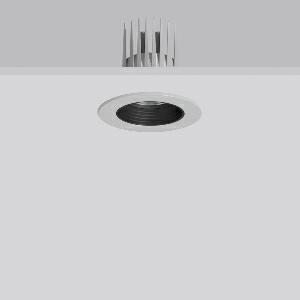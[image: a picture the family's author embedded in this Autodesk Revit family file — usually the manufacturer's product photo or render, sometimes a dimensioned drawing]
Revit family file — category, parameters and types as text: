
# Revit family: heledon_mini_e_901746_004_2_a7c6
name_source: partatom
category: Lighting Fixtures
units: mm (PartAtom-declared; Revit-internal decimal feet)

## family parameters
Cut with Voids When Loaded = No
Host = Face
Light Source = No
Part Type = Normal
Room Calculation Point = No
Round Connector Dimension = Use Diameter
Shared = No

## types (1)
- HELEDON mini E (1 x LED Modul 927, 2150 lm, 2700)
    Apparent Load = 20 VA
    Approval mark = CE
    CIE Flux Codes = 80 99 100 100 100
    Color Rendering = 92
    Color Temperature = 2700
    Default Elevation = 1800 mm
    Description = Series: HELEDON mini
Round recessed downlight. Housing: die-cast aluminium, powder-coated. Black plastic ring and recessed LED to prevent glare from the side. Optical assembly with lens made of plastic (polycarbonate) for the best homogeneous light distribution - can be changed without tools. Best colour rendering index Ra>90. Suitable for Recessed ceiling mounting. Installation without tools thanks to spring fastening system. Including separate LED converter with connecting cable 600 mm.High quality converter without flickering and stroboscopic effect. Through-wiring box (5 pole) available as accessory. The following accessories can be mounted without use of tools: interchangeable lenses, decorative glasses, honeycomb louvre, clear and frosted diffusers, white interchangeable plastic ring. 
Colour: silver
Diameter: 124 mm
Height: 3 mm
Cut-out diameter: 114 mm
Recess height: 170 mm
Luminaire: recess height: 120 mm
Lamp: LED
Socket: without socket
Colour temperature: 2700K
Colour rendering index (CRI): 92
System power: 20 W
Rated luminous flux: 2150 lm
Luminous efficiency: 108 lm/W
Control gear: Regulated power supply
Protection class: II
Type of protection: IP 20
    Height = 0 mm  [stored 0 ft]
    Lamp = 1 x LED Modul 927
    Lamp Light Flux = 2150 lm
    Lamp count = 1
    Length = 124 mm  [stored 0.406824 ft]
    Lifetime = 50000 h
    Luminous efficacy = 108 lm/W
    Manufacturer = RZB
    ModVariant = No
    Model = 901746.004.2
    Mounting Place = Ceiling
    Mounting Type = Recessed
    Number of Poles = 1
    OnlyDefault = Yes
    Power Factor = 1
    Product Name = HELEDON mini E
    Product group = Recessed downlights
    ProductGroupID = 402
    Protection Class = Protection class II
    Protection Degree = IP 20
    RLX_Detail_Level = 1
    RLX_Emergency_Light_Flux = 0 lm
    RLX_Emergency_Type = 0
    RLX_Emergency_Type_DB = No
    RlxData = <blob elided: 127645 chars, md5=7dd7c361>
    Socket = socket
    Standby Power = 0 W
    System Light Flux = 2150 lm
    System Power = 20 W
    Type Comments = Product without accessories
    Type Image = 901656.004.jpg
    URL = http://relux.com
    VarID = ---
    Voltage = 230 V
    Voltage Range = 220-240 V
    Weight = 0.00 kg
    Width = 0 mm  [stored 0 ft]

note: [stored X ft] marks values corroborated as IEEE doubles in the binary element streams (Revit-internal decimal feet)

## geometry (parser evidence)
native form markers: Blend x4, Sweep x9
no freeform markers — native parametric forms only
